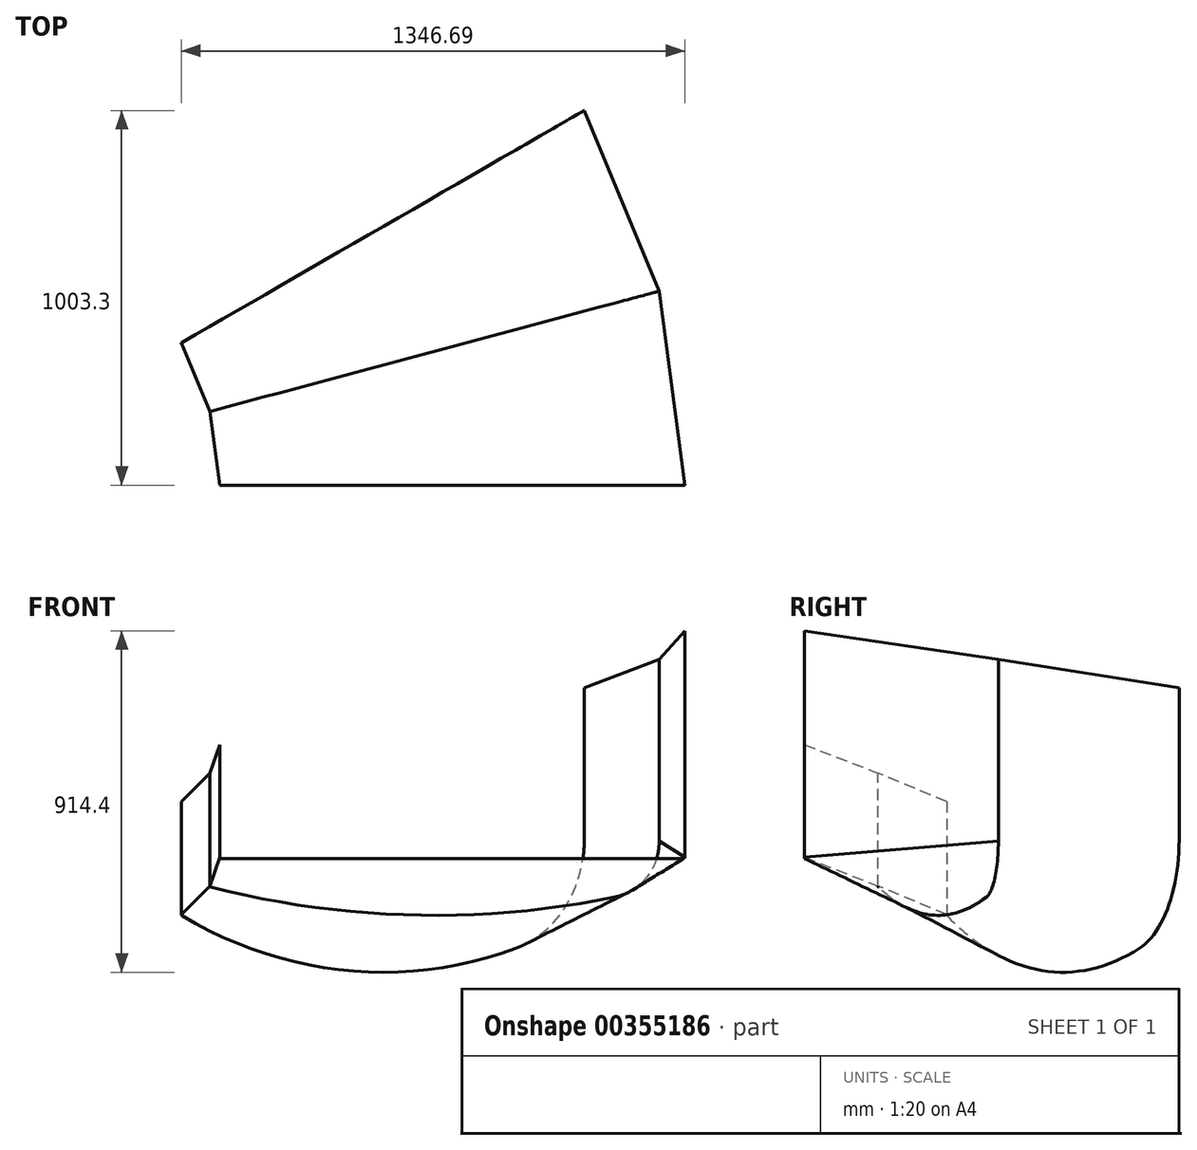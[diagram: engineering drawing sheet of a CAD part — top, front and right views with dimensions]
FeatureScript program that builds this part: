
annotation { "Feature Type Name" : "Feature", "Feature Type Description" : "" }
export const myFeature = defineFeature(function(context is Context, id is Id, definition is map)
    precondition{}
    {
        {
            var Q0;
            Q0=qCreatedBy(makeId("Front.planeOp"),FACE);
            var sketch = newSketch(context, id + "F0", { "sketchPlane" : qUnion([Q0])});
            skLineSegment(sketch, "E0", {"start": v(762, 304.8) * mm, "end": v(762, 3.17) * mm});
            skLineSegment(sketch, "E1", {"start": v(765.18, 0) * mm, "end": v(2003.42, 0) * mm});
            skLineSegment(sketch, "E2", {"start": v(2006.6, 3.17) * mm, "end": v(2006.6, 609.6) * mm});
            skLineSegment(sketch, "E3", {"start": v(0, 0) * mm, "end": v(0, 948.65) * mm, "construction": true});
            skPoint(sketch, "E4.visualSharp", {"position": v(2006.6, 0) * mm});
            skArc(sketch, "E4.filletArc", {"start": v(2003.42, 0) * mm, "mid": v(2005.67, 0.93) * mm, "end": v(2006.6, 3.17) * mm});
            skPoint(sketch, "E5.visualSharp", {"position": v(762, 0) * mm});
            skArc(sketch, "E5.filletArc", {"start": v(762, 3.17) * mm, "mid": v(762.93, 0.93) * mm, "end": v(765.18, 0) * mm});
            skSolve(sketch);
        }
        {
            var Q0;
            Q0=sQuery(id+"F0.wireOp",EDGE,"E3");
            cPlane(context, id + "F1", {"entities" : qUnion([Q0]), "cplaneType" : CPlaneType.LINE_ANGLE, "offset" : 25.4 * mm, "angle" : 105 * degree, "width" : 152.4 * mm, "height" : 152.4 * mm});
        }
        {
            var Q0;
            Q0=qCreatedBy(id+"F1.planeOp",FACE);
            var sketch = newSketch(context, id + "F2", { "sketchPlane" : qUnion([Q0])});
            skLineSegment(sketch, "E6", {"start": v(-2006.6, 533.4) * mm, "end": v(-2006.6, 45.93) * mm});
            skLineSegment(sketch, "E7", {"start": v(-2006.6, -76.2) * mm, "end": v(-762, -76.2) * mm, "construction": true});
            skLineSegment(sketch, "E8", {"start": v(-762, -73.72) * mm, "end": v(-762, 228.6) * mm});
            skArc(sketch, "E9", {"start": v(-1883.7, -103.59) * mm, "mid": v(-1322.59, -151.66) * mm, "end": v(-764.41, -76.8) * mm});
            skPoint(sketch, "E10.visualSharp", {"position": v(-2006.6, -76.2) * mm});
            skArc(sketch, "E10.filletArc", {"start": v(-2006.6, 45.93) * mm, "mid": v(-1971.93, -50.84) * mm, "end": v(-1883.7, -103.59) * mm});
            skPoint(sketch, "E11.visualSharp", {"position": v(-762, -76.2) * mm});
            skArc(sketch, "E11.filletArc", {"start": v(-764.41, -76.8) * mm, "mid": v(-762.67, -75.67) * mm, "end": v(-762, -73.72) * mm});
            skSolve(sketch);
        }
        {
            var Q0;
            Q0=sQuery(id+"F0.wireOp",EDGE,"E3");
            cPlane(context, id + "F3", {"entities" : qUnion([Q0]), "cplaneType" : CPlaneType.LINE_ANGLE, "offset" : 25.4 * mm, "angle" : 60 * degree, "oppositeDirection" : true, "width" : 152.4 * mm, "height" : 152.4 * mm});
        }
        {
            var Q0;
            Q0=qCreatedBy(id+"F3.planeOp",FACE);
            var sketch = newSketch(context, id + "F4", { "sketchPlane" : qUnion([Q0])});
            skLineSegment(sketch, "E12", {"start": v(762, 152.4) * mm, "end": v(762, -150.47) * mm});
            skLineSegment(sketch, "E13", {"start": v(762, -152.4) * mm, "end": v(2003.42, -152.4) * mm, "construction": true});
            skLineSegment(sketch, "E14", {"start": v(2006.6, 49.55) * mm, "end": v(2006.6, 457.2) * mm});
            skPoint(sketch, "E15.visualSharp", {"position": v(2006.6, -152.4) * mm});
            skPoint(sketch, "E16.visualSharp", {"position": v(762, -152.4) * mm});
            skArc(sketch, "E17", {"start": v(763.71, -153.3) * mm, "mid": v(1270.46, -299.98) * mm, "end": v(1794.68, -240.75) * mm});
            skArc(sketch, "E18.filletArc", {"start": v(1794.68, -240.75) * mm, "mid": v(1947.98, -130.16) * mm, "end": v(2006.6, 49.55) * mm});
            skArc(sketch, "E19.filletArc", {"start": v(762, -150.47) * mm, "mid": v(762.46, -152.12) * mm, "end": v(763.71, -153.3) * mm});
            skSolve(sketch);
        }
        {
            var Q0;
            Q0 = qSketchRegion(id + "F0", true);
            var Q1;
            Q1 = qSketchRegion(id + "F2", true);
            var Q2;
            Q2 = qConstructionFilter(qBodyType(qCreatedBy(id + "F0" ,EDGE), BodyType.WIRE), ConstructionObject.NO);
            var Q3;
            Q3 = qConstructionFilter(qBodyType(qCreatedBy(id + "F2" ,EDGE), BodyType.WIRE), ConstructionObject.NO);
            var Q4;
            Q4=sQuery(id+"F2.wireOp",VERTEX,"E9.end");
            var Q5;
            Q5=sQuery(id+"F0.wireOp",VERTEX,"E1.start");
            loft(context, id + "F5", {"bodyType" : ToolBodyType.SURFACE, "sheetProfilesArray" : [{ "sheetProfileEntities" : qUnion([Q0]) }, { "sheetProfileEntities" : qUnion([Q1]) }], "wireProfilesArray" : [{ "wireProfileEntities" : qUnion([Q2]) }, { "wireProfileEntities" : qUnion([Q3]) }], "matchConnections" : true, "connections" : [{ "connectionEntities" : qUnion([Q4, Q5]), "connectionEdgeQueries" : qUnion([]), "connectionEdgeParameters" : [] }]});
        }
        {
            var Q0;
            Q0 = qSketchRegion(id + "F2", true);
            var Q1;
            Q1 = qSketchRegion(id + "F4", true);
            var Q2;
            Q2 = qConstructionFilter(qBodyType(qCreatedBy(id + "F4" ,EDGE), BodyType.WIRE), ConstructionObject.NO);
            var Q3;
            Q3 = qConstructionFilter(qBodyType(qCreatedBy(id + "F2" ,EDGE), BodyType.WIRE), ConstructionObject.NO);
            var Q4;
            Q4=sQuery(id+"F4.wireOp",VERTEX,"E19.filletArc.start");
            var Q5;
            Q5=makeQuery(id+"F5.opLoft","MID_CAP_VERTEX",VERTEX,{"disambiguationData":[OSD([sQuery(id+"F2.wireOp",VERTEX,"E11.filletArc.end")])],"capPos":1.0});
            loft(context, id + "F6", {"bodyType" : ToolBodyType.SURFACE, "sheetProfilesArray" : [{ "sheetProfileEntities" : qUnion([Q0]) }, { "sheetProfileEntities" : qUnion([Q1]) }], "wireProfilesArray" : [{ "wireProfileEntities" : qUnion([Q2]) }, { "wireProfileEntities" : qUnion([Q3]) }], "connections" : [{ "connectionEntities" : qUnion([Q4, Q5]), "connectionEdgeQueries" : qUnion([]), "connectionEdgeParameters" : [] }]});
        }
    });
